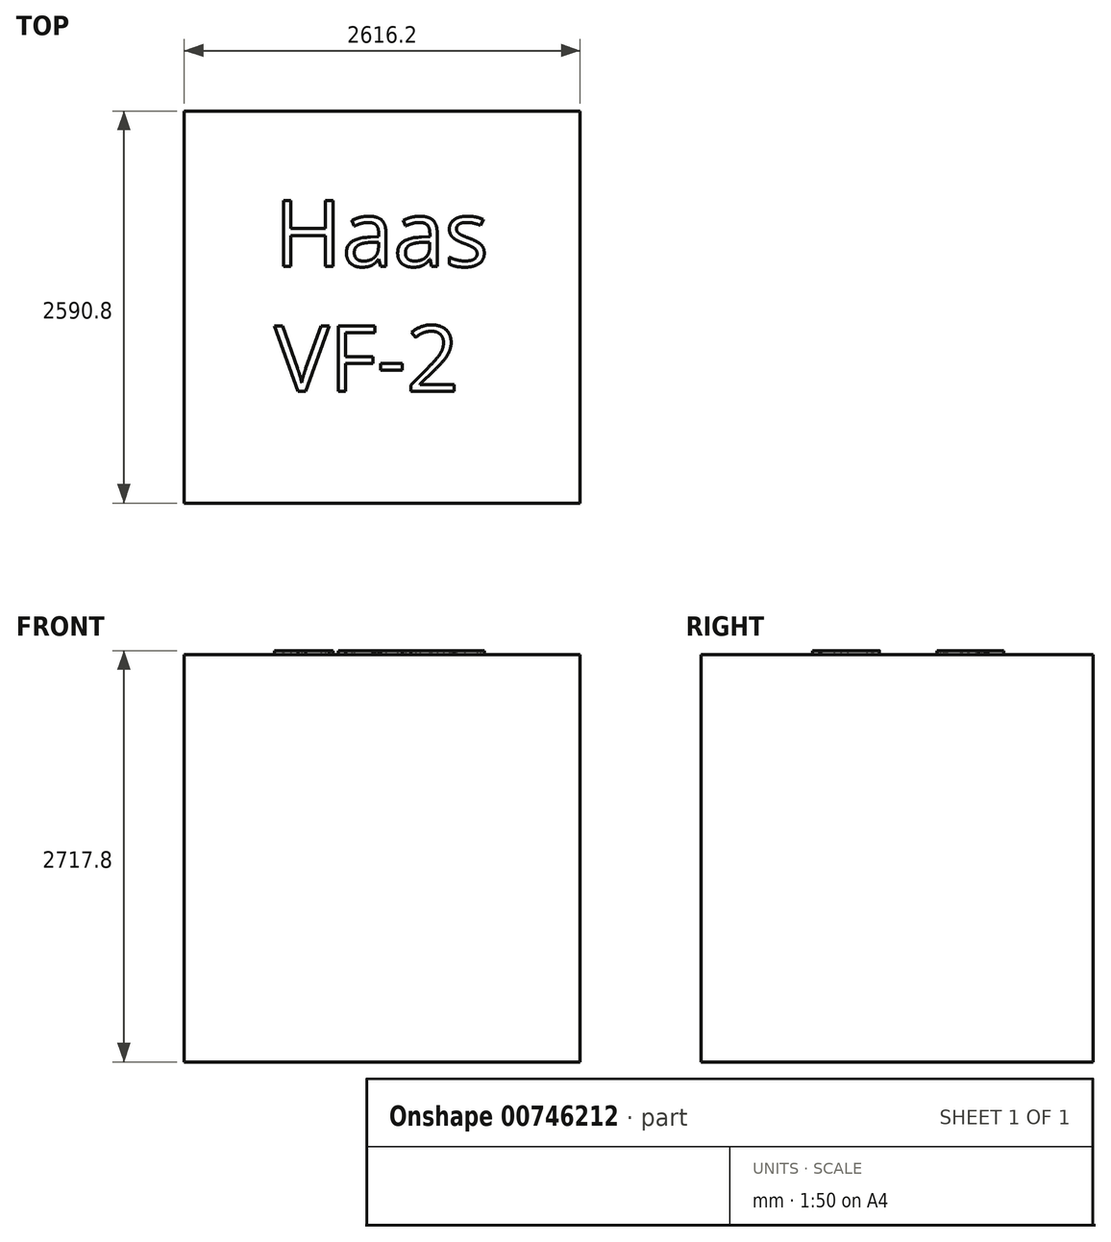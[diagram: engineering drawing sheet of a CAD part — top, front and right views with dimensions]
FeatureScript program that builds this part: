
annotation { "Feature Type Name" : "Feature", "Feature Type Description" : "" }
export const myFeature = defineFeature(function(context is Context, id is Id, definition is map)
    precondition{}
    {
        {
            var Q0;
            Q0=qCreatedBy(makeId("Top.planeOp"),FACE);
            var sketch = newSketch(context, id + "F0", { "sketchPlane" : qUnion([Q0])});
            skLineSegment(sketch, "E0.bottom", {"start": v(1308.1, -1295.4) * mm, "end": v(-1308.1, -1295.4) * mm});
            skLineSegment(sketch, "E0.top", {"start": v(1308.1, 1295.4) * mm, "end": v(-1308.1, 1295.4) * mm});
            skLineSegment(sketch, "E0.left", {"start": v(1308.1, -1295.4) * mm, "end": v(1308.1, 1295.4) * mm});
            skLineSegment(sketch, "E0.right", {"start": v(-1308.1, -1295.4) * mm, "end": v(-1308.1, 1295.4) * mm});
            skPoint(sketch, "E0.middle", {"position": v(0, 0) * mm});
            skSolve(sketch);
        }
        {
            var Q0;
            Q0 = qSketchRegion(id + "F0", true);
            extrude(context, id + "F1", {"entities" : qUnion([Q0]), "depth" : 2692.4 * mm, "offsetDistance" : 25.4 * mm});
        }
        {
            var Q0;
            Q0=makeQuery(id+"F1.opExtrude","CAP_FACE",FACE,{"disambiguationData":[OSD([sQuery(id+"F0.wireOp",EDGE,"E0.bottom"),sQuery(id+"F0.wireOp",EDGE,"E0.top"),sQuery(id+"F0.wireOp",EDGE,"E0.left"),sQuery(id+"F0.wireOp",EDGE,"E0.right")])],"isStart":false});
            var sketch = newSketch(context, id + "F2", { "sketchPlane" : qUnion([Q0])});
            skText(sketch, "E1", { "text": "Haas\nVF-2", "fontName": "OpenSans-Regular.ttf"});
            const initialGuessF2  = {"E1": [-0.7135, 0.26865, 1, 0, 0.43796]};
            skSetInitialGuess(sketch, initialGuessF2);
            skSolve(sketch);
        }
        {
            var Q0;
            Q0 = qSketchRegion(id + "F2", true);
            extrude(context, id + "F3", {"entities" : qUnion([Q0]), "operationType" : NewBodyOperationType.ADD, "depth" : 25.4 * mm, "offsetDistance" : 25.4 * mm});
        }
    });
